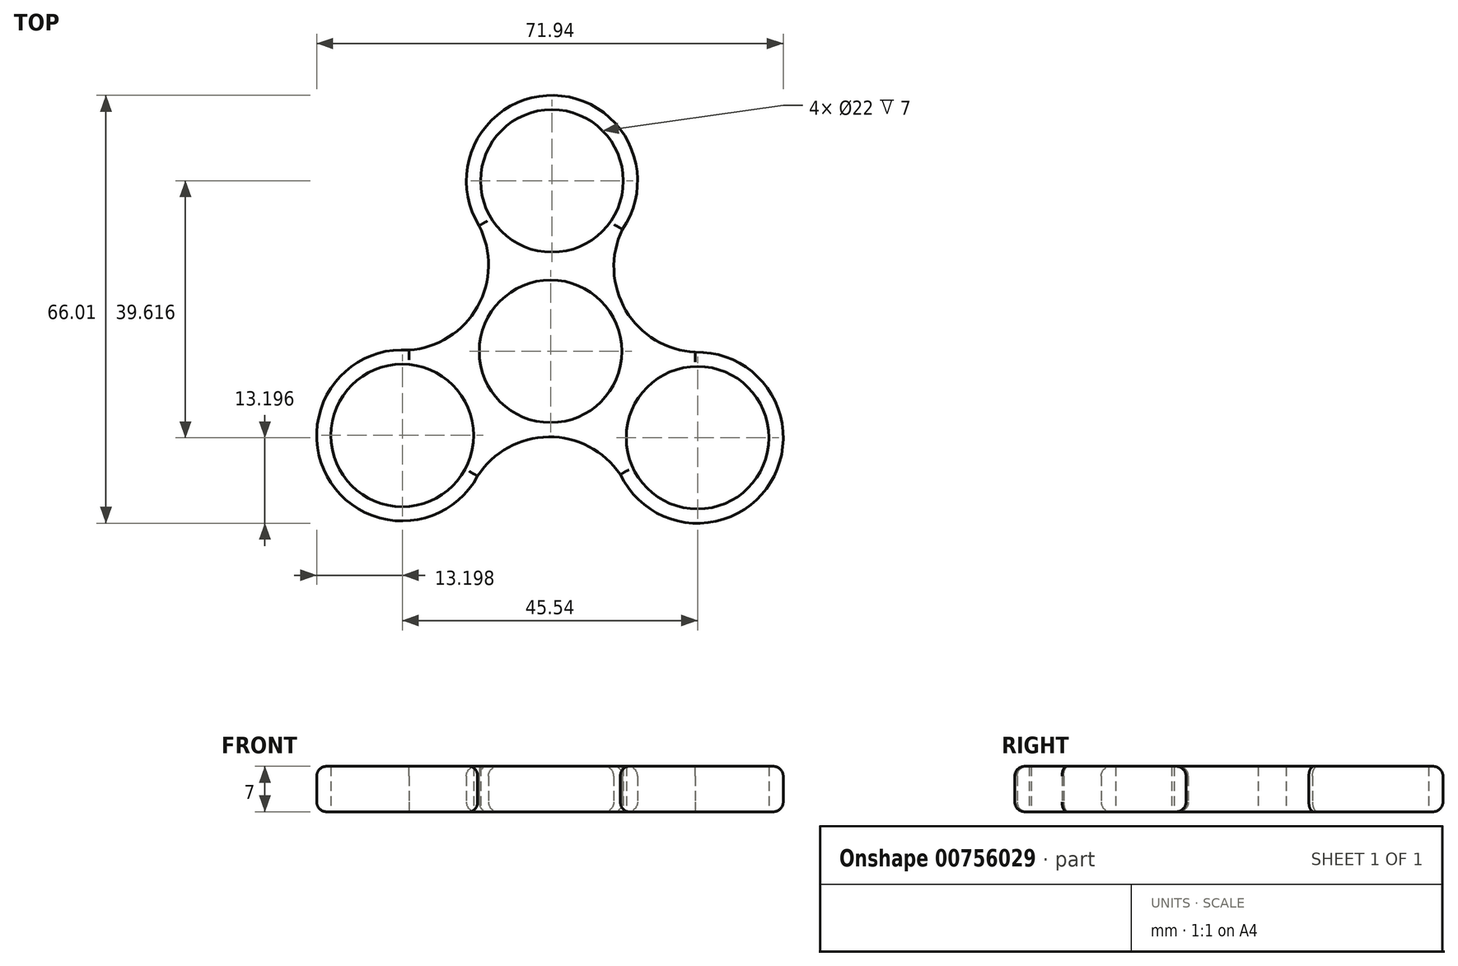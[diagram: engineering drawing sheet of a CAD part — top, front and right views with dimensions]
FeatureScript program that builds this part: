
annotation { "Feature Type Name" : "Feature", "Feature Type Description" : "" }
export const myFeature = defineFeature(function(context is Context, id is Id, definition is map)
    precondition{}
    {
        {
            var Q0;
            Q0=qCreatedBy(makeId("Top.planeOp"),FACE);
            var sketch = newSketch(context, id + "F0", { "sketchPlane" : qUnion([Q0])});
            skCircle(sketch, "E0", {"center": v(0, 0) * mm, "radius": 11 * mm});
            skCircle(sketch, "E1", {"center": v(0.2, 26.3) * mm, "radius": 11 * mm});
            skArc(sketch, "E2", {"start": v(11.08, 18.81) * mm, "mid": v(0.54, 39.49) * mm, "end": v(-11.04, 19.38) * mm});
            skCircle(sketch, "E3.1.1", {"center": v(-22.87, -12.97) * mm, "radius": 11 * mm});
            skArc(sketch, "E3.2.0", {"start": v(10.75, -19) * mm, "mid": v(33.93, -20.21) * mm, "end": v(22.3, -0.13) * mm});
            skCircle(sketch, "E3.2.1", {"center": v(22.67, -13.32) * mm, "radius": 11 * mm});
            skArc(sketch, "E4", {"start": v(11.08, 18.81) * mm, "mid": v(11.6, 6.32) * mm, "end": v(22.3, -0.13) * mm});
            skPoint(sketch, "E4.endSnap0", {"position": v(22.3, 12.64) * mm});
            skArc(sketch, "E5.1.0", {"start": v(-21.83, 0.19) * mm, "mid": v(-11.27, 6.88) * mm, "end": v(-11.04, 19.38) * mm});
            skArc(sketch, "E5.2.0", {"start": v(10.75, -19) * mm, "mid": v(-0.32, -13.2) * mm, "end": v(-11.26, -19.25) * mm});
            skPoint(sketch, "E6.trimOffspring.end.orphan", {"position": v(44.6, 25.29) * mm});
            skArc(sketch, "E7.trimOffspring", {"start": v(-21.83, 0.19) * mm, "mid": v(-34.47, -19.28) * mm, "end": v(-11.26, -19.25) * mm});
            skSolve(sketch);
        }
        {
            var Q0;
            Q0=makeQuery(id+"F0.imprint","IMPRINT",FACE,{"disambiguationData":[TD([[makeQuery(id+"F0.imprint","IMPRINT",EDGE,{"derivedFrom":sQuery(id+"F0.wireOp",EDGE,"E0")}),-1.0]])]});
            extrude(context, id + "F1", {"entities" : qUnion([Q0]), "depth" : 7 * mm, "offsetDistance" : 25 * mm});
        }
        {
            var Q0;
            Q0=makeQuery(id+"F1.opExtrude","CAP_EDGE",EDGE,{"disambiguationData":[OSD([sQuery(id+"F0.wireOp",EDGE,"E2")])],"isStart":false});
            var Q1;
            Q1=makeQuery(id+"F1.opExtrude","CAP_EDGE",EDGE,{"disambiguationData":[OSD([sQuery(id+"F0.wireOp",EDGE,"E5.1.0")])],"isStart":false});
            var Q2;
            Q2=makeQuery(id+"F1.opExtrude","CAP_EDGE",EDGE,{"disambiguationData":[OSD([sQuery(id+"F0.wireOp",EDGE,"E7.trimOffspring")])],"isStart":false});
            var Q3;
            Q3=makeQuery(id+"F1.opExtrude","CAP_EDGE",EDGE,{"disambiguationData":[OSD([sQuery(id+"F0.wireOp",EDGE,"E5.2.0")])],"isStart":false});
            var Q4;
            Q4=makeQuery(id+"F1.opExtrude","CAP_EDGE",EDGE,{"disambiguationData":[OSD([sQuery(id+"F0.wireOp",EDGE,"E3.2.0")])],"isStart":false});
            var Q5;
            Q5=makeQuery(id+"F1.opExtrude","CAP_EDGE",EDGE,{"disambiguationData":[OSD([sQuery(id+"F0.wireOp",EDGE,"E4")])],"isStart":false});
            fillet(context, id + "F2", {"entities" : qUnion([Q0, Q1, Q2, Q3, Q4, Q5]), "radius" : 1.5 * mm, "tangentPropagation" : true, "allowEdgeOverflow" : false});
        }
        {
            var Q0;
            Q0=makeQuery(id+"F1.opExtrude","CAP_EDGE",EDGE,{"disambiguationData":[OSD([sQuery(id+"F0.wireOp",EDGE,"E5.2.0")])],"isStart":true});
            var Q1;
            Q1=makeQuery(id+"F1.opExtrude","CAP_EDGE",EDGE,{"disambiguationData":[OSD([sQuery(id+"F0.wireOp",EDGE,"E7.trimOffspring")])],"isStart":true});
            var Q2;
            Q2=makeQuery(id+"F1.opExtrude","CAP_EDGE",EDGE,{"disambiguationData":[OSD([sQuery(id+"F0.wireOp",EDGE,"E5.1.0")])],"isStart":true});
            var Q3;
            Q3=makeQuery(id+"F1.opExtrude","CAP_EDGE",EDGE,{"disambiguationData":[OSD([sQuery(id+"F0.wireOp",EDGE,"E2")])],"isStart":true});
            var Q4;
            Q4=makeQuery(id+"F1.opExtrude","CAP_EDGE",EDGE,{"disambiguationData":[OSD([sQuery(id+"F0.wireOp",EDGE,"E4")])],"isStart":true});
            var Q5;
            Q5=makeQuery(id+"F1.opExtrude","CAP_EDGE",EDGE,{"disambiguationData":[OSD([sQuery(id+"F0.wireOp",EDGE,"E3.2.0")])],"isStart":true});
            fillet(context, id + "F3", {"entities" : qUnion([Q0, Q1, Q2, Q3, Q4, Q5]), "radius" : 1.5 * mm, "tangentPropagation" : true, "allowEdgeOverflow" : false});
        }
    });
